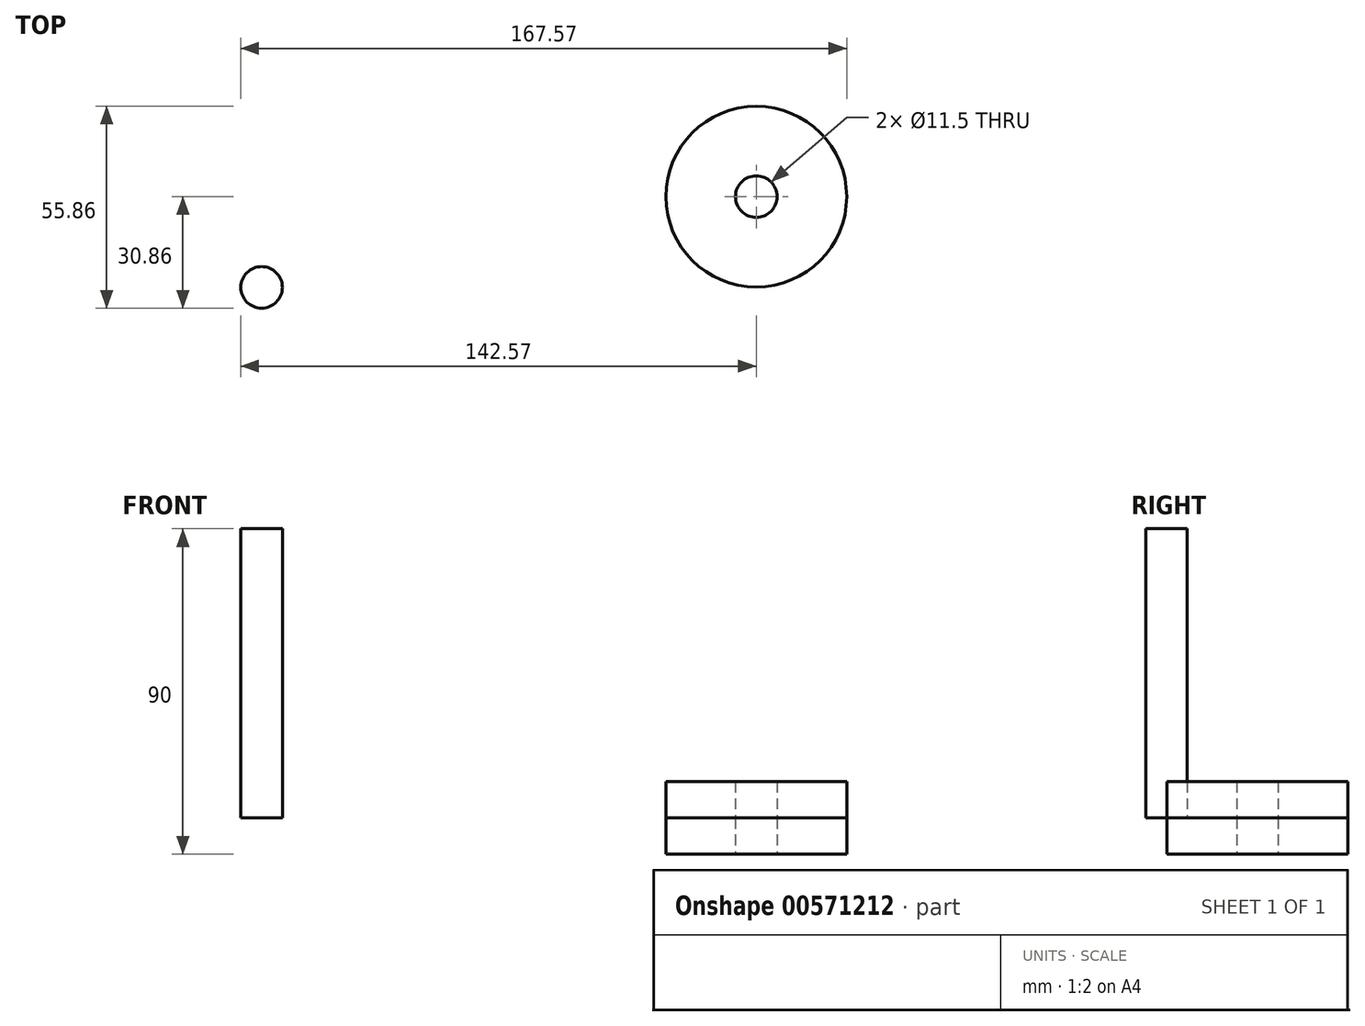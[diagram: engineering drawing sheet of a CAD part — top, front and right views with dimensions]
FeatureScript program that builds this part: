
annotation { "Feature Type Name" : "Feature", "Feature Type Description" : "" }
export const myFeature = defineFeature(function(context is Context, id is Id, definition is map)
    precondition{}
    {
        {
            var Q0;
            Q0=qCreatedBy(makeId("Top.planeOp"),FACE);
            var sketch = newSketch(context, id + "F0", { "sketchPlane" : qUnion([Q0])});
            skCircle(sketch, "E0", {"center": v(0, 0) * mm, "radius": 25 * mm});
            skSolve(sketch);
        }
        {
            var Q0;
            Q0 = qSketchRegion(id + "F0", true);
            extrude(context, id + "F1", {"entities" : qUnion([Q0]), "depth" : 10 * mm, "offsetDistance" : 25.4 * mm});
        }
        {
            var Q0;
            Q0 = qSketchRegion(id + "F0", true);
            extrude(context, id + "F2", {"entities" : qUnion([Q0]), "oppositeDirection" : true, "depth" : 10 * mm, "offsetDistance" : 25.4 * mm});
        }
        {
            var Q0;
            Q0=qCreatedBy(makeId("Top.planeOp"),FACE);
            var sketch = newSketch(context, id + "F3", { "sketchPlane" : qUnion([Q0])});
            skCircle(sketch, "E1", {"center": v(0, 0) * mm, "radius": 5.75 * mm});
            skSolve(sketch);
        }
        {
            var Q0;
            Q0 = qSketchRegion(id + "F3", true);
            extrude(context, id + "F4", {"entities" : qUnion([Q0]), "operationType" : NewBodyOperationType.REMOVE, "depth" : 10 * mm, "offsetDistance" : 25.4 * mm, "hasSecondDirection" : true, "secondDirectionOppositeDirection" : true, "secondDirectionDepth" : 10 * mm});
        }
        {
            var Q0;
            Q0=qCreatedBy(makeId("Top.planeOp"),FACE);
            var sketch = newSketch(context, id + "F5", { "sketchPlane" : qUnion([Q0])});
            skCircle(sketch, "E2", {"center": v(-136.82, -25.1) * mm, "radius": 5.75 * mm});
            skSolve(sketch);
        }
        {
            var Q0;
            Q0 = qSketchRegion(id + "F5", true);
            extrude(context, id + "F6", {"entities" : qUnion([Q0]), "depth" : 80 * mm, "offsetDistance" : 25.4 * mm});
        }
    });
